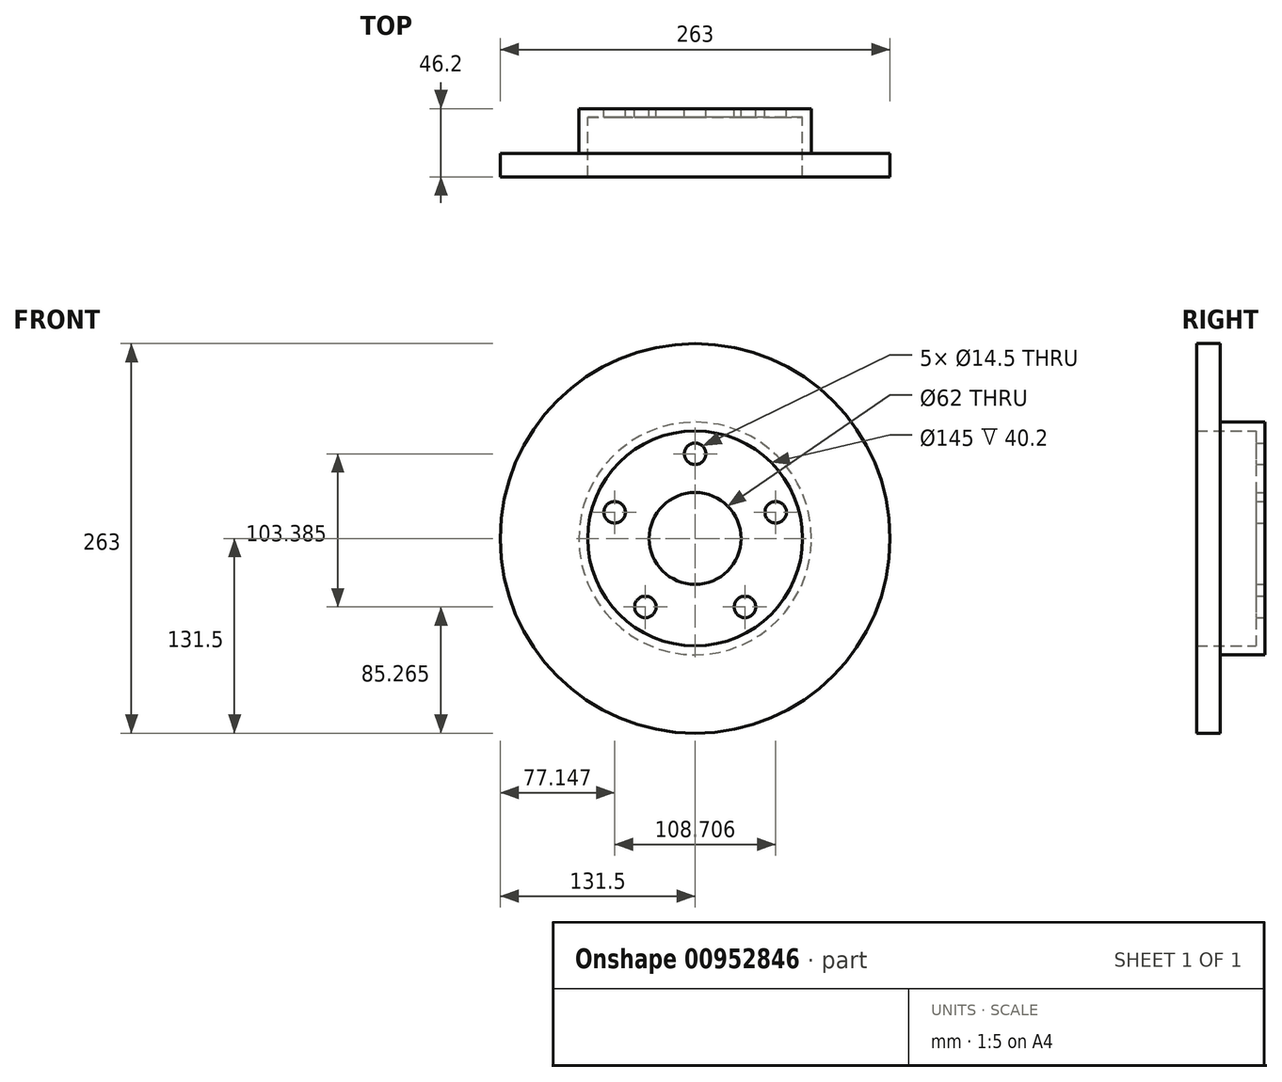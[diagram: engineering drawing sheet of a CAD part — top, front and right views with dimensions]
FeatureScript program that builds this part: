
annotation { "Feature Type Name" : "Feature", "Feature Type Description" : "" }
export const myFeature = defineFeature(function(context is Context, id is Id, definition is map)
    precondition{}
    {
        {
            var Q0;
            Q0=qCreatedBy(makeId("Right.planeOp"),FACE);
            var sketch = newSketch(context, id + "F0", { "sketchPlane" : qUnion([Q0])});
            skLineSegment(sketch, "E0", {"start": v(0, 0) * mm, "end": v(-132.22, 0) * mm, "construction": true});
            skLineSegment(sketch, "E1", {"start": v(0, 31) * mm, "end": v(0, 72.5) * mm});
            skLineSegment(sketch, "E2", {"start": v(0, 72.5) * mm, "end": v(-40.2, 72.5) * mm});
            skLineSegment(sketch, "E3", {"start": v(-40.2, 72.5) * mm, "end": v(-40.2, 131.5) * mm});
            skLineSegment(sketch, "E4", {"start": v(-40.2, 131.5) * mm, "end": v(-24.2, 131.5) * mm});
            skLineSegment(sketch, "E5", {"start": v(-24.2, 131.5) * mm, "end": v(-24.2, 78.5) * mm});
            skLineSegment(sketch, "E6", {"start": v(-24.2, 78.5) * mm, "end": v(6, 78.5) * mm});
            skLineSegment(sketch, "E7", {"start": v(6, 78.5) * mm, "end": v(6, 31) * mm});
            skLineSegment(sketch, "E8", {"start": v(6, 31) * mm, "end": v(0, 31) * mm});
            skSolve(sketch);
        }
        {
            var Q0;
            Q0 = qSketchRegion(id + "F0", true);
            var Q1;
            Q1=sQuery(id+"F0.wireOp",EDGE,"E0");
            revolve(context, id + "F1", {"surfaceOperationType" : NewSurfaceOperationType.NEW, "entities" : qUnion([Q0]), "axis" : qUnion([Q1]), "revolveType" : RevolveType.FULL});
        }
        {
            var Q0;
            Q0=makeQuery(id+"F1.opRevolve","SWEPT_FACE",FACE,{"disambiguationData":[OSD([sQuery(id+"F0.wireOp",EDGE,"E7")])]});
            var sketch = newSketch(context, id + "F2", { "sketchPlane" : qUnion([Q0])});
            skCircle(sketch, "E9.cCircle", {"center": v(0, 0) * mm, "radius": 57.15 * mm, "construction": true});
            skLineSegment(sketch, "E9.0", {"start": v(0, 57.15) * mm, "end": v(54.35, 17.66) * mm});
            skLineSegment(sketch, "E9.1", {"start": v(54.35, 17.66) * mm, "end": v(33.6, -46.24) * mm});
            skLineSegment(sketch, "E9.2", {"start": v(33.6, -46.24) * mm, "end": v(-33.6, -46.24) * mm});
            skLineSegment(sketch, "E9.3", {"start": v(-33.6, -46.24) * mm, "end": v(-54.35, 17.66) * mm});
            skLineSegment(sketch, "E9.4", {"start": v(-54.35, 17.66) * mm, "end": v(0, 57.15) * mm});
            skSolve(sketch);
        }
        {
            var Q0;
            Q0=sQuery(id+"F2.wireOp",VERTEX,"E9.0.start");
            var Q1;
            Q1=sQuery(id+"F2.wireOp",VERTEX,"E9.0.end");
            var Q2;
            Q2=sQuery(id+"F2.wireOp",VERTEX,"E9.1.end");
            var Q3;
            Q3=sQuery(id+"F2.wireOp",VERTEX,"E9.2.end");
            var Q4;
            Q4=sQuery(id+"F2.wireOp",VERTEX,"E9.3.end");
            var Q5;
            Q5=makeQuery(id+"F1.opRevolve","SWEPT_BODY",BODY,{"disambiguationData":[OSD([sQuery(id+"F0.wireOp",EDGE,"E1"),sQuery(id+"F0.wireOp",EDGE,"E2"),sQuery(id+"F0.wireOp",EDGE,"E3"),sQuery(id+"F0.wireOp",EDGE,"E4"),sQuery(id+"F0.wireOp",EDGE,"E5"),sQuery(id+"F0.wireOp",EDGE,"E6"),sQuery(id+"F0.wireOp",EDGE,"E7"),sQuery(id+"F0.wireOp",EDGE,"E8")])]});
            hole(context, id + "F3", {"style" : HoleStyle.SIMPLE, "endStyle" : HoleEndStyle.THROUGH, "standardTappedOrClearance" : lookupTablePath({ "standard" : "ISO", "size" : "14.5", "type" : "Drilled" }), "standardBlindInLast" : lookupTablePath({ "standard" : "ISO", "size" : "14.5", "type" : "Drilled" }), "holeDiameter" : 14.5 * mm, "majorDiameter" : 5 * mm, "isTappedThrough" : true, "tappedDepth" : 12 * mm, "tapClearance" : 3, "startFromSketch" : true, "locations" : qUnion([Q0, Q1, Q2, Q3, Q4]), "scope" : qUnion([Q5])});
        }
    });
